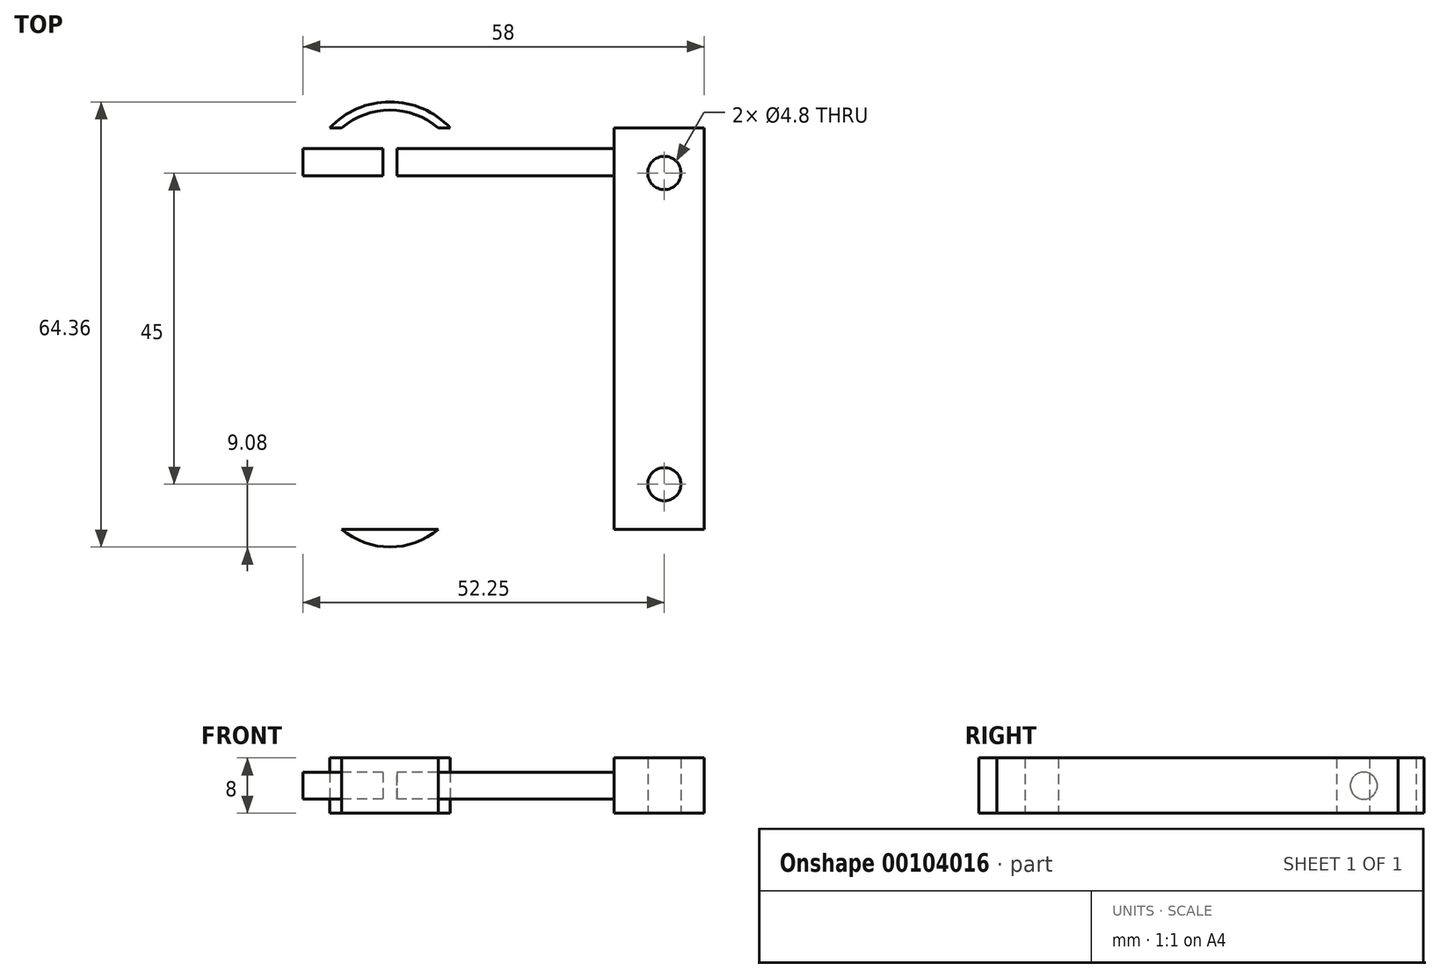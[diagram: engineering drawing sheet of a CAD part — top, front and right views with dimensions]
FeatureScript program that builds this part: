
annotation { "Feature Type Name" : "Feature", "Feature Type Description" : "" }
export const myFeature = defineFeature(function(context is Context, id is Id, definition is map)
    precondition{}
    {
        {
            var Q0;
            Q0=qCreatedBy(makeId("Top.planeOp"),FACE);
            var sketch = newSketch(context, id + "F0", { "sketchPlane" : qUnion([Q0])});
            skLineSegment(sketch, "E0.bottom", {"start": v(29, 29) * mm, "end": v(-29, 29) * mm});
            skLineSegment(sketch, "E0.top", {"start": v(29, -29) * mm, "end": v(-29, -29) * mm});
            skLineSegment(sketch, "E0.left", {"start": v(29, 29) * mm, "end": v(29, -29) * mm});
            skLineSegment(sketch, "E0.right", {"start": v(-29, 29) * mm, "end": v(-29, -29) * mm});
            skPoint(sketch, "E0.middle", {"position": v(0, 0) * mm});
            skCircle(sketch, "E1", {"center": v(-23.25, 0) * mm, "radius": 2.4 * mm});
            skCircle(sketch, "E2", {"center": v(-23.25, 0) * mm, "radius": 11.5 * mm, "construction": true});
            skLineSegment(sketch, "E3", {"start": v(0, 29) * mm, "end": v(0, -29) * mm, "construction": true});
            skCircle(sketch, "E4.MirrorC", {"center": v(23.25, 0) * mm, "radius": 11.5 * mm, "construction": true});
            skCircle(sketch, "E5", {"center": v(23.25, 22.5) * mm, "radius": 2.4 * mm});
            skLineSegment(sketch, "E6", {"start": v(0, 0) * mm, "end": v(29, 0) * mm, "construction": true});
            skCircle(sketch, "E7.MirrorC", {"center": v(23.25, -22.5) * mm, "radius": 2.4 * mm});
            skLineSegment(sketch, "E8", {"start": v(-17.4, 29) * mm, "end": v(-17.4, -29) * mm});
            skLineSegment(sketch, "E9", {"start": v(-15.4, 29) * mm, "end": v(-15.4, -29) * mm});
            skLineSegment(sketch, "E10", {"start": v(-7.76, 17) * mm, "end": v(12.59, 17) * mm});
            skLineSegment(sketch, "E11", {"start": v(12.59, 17) * mm, "end": v(12.59, 14.52) * mm});
            skLineSegment(sketch, "E12", {"start": v(12.59, 14.52) * mm, "end": v(-7.76, 7) * mm});
            skLineSegment(sketch, "E13", {"start": v(-7.76, 7) * mm, "end": v(-7.76, 17) * mm});
            skLineSegment(sketch, "E14.MirrorCS", {"start": v(12.59, -14.52) * mm, "end": v(-7.76, -7) * mm});
            skLineSegment(sketch, "E15.MirrorCS", {"start": v(12.59, -17) * mm, "end": v(12.59, -14.52) * mm});
            skLineSegment(sketch, "E16.MirrorCS", {"start": v(-7.76, -17) * mm, "end": v(12.59, -17) * mm});
            skLineSegment(sketch, "E17.MirrorCS", {"start": v(-7.76, -7) * mm, "end": v(-7.76, -17) * mm});
            skArc(sketch, "E18", {"start": v(-9.41, 29) * mm, "mid": v(-16.4, 31.58) * mm, "end": v(-23.38, 29) * mm});
            skArc(sketch, "E19", {"start": v(-7.68, 29) * mm, "mid": v(-16.4, 32.78) * mm, "end": v(-25.11, 29) * mm});
            skLineSegment(sketch, "E20", {"start": v(-17.4, 20.84) * mm, "end": v(-15.4, 20.84) * mm, "construction": true});
            skArc(sketch, "E21.MirrorCS", {"start": v(-9.41, -29) * mm, "mid": v(-16.4, -31.58) * mm, "end": v(-23.38, -29) * mm});
            skArc(sketch, "E22.MirrorCS", {"start": v(-7.68, -29) * mm, "mid": v(-16.4, -32.78) * mm, "end": v(-25.11, -29) * mm});
            skSolve(sketch);
        }
        {
            var Q0;
            {var subQ0=sQuery(id+"F0.wireOp",EDGE,"E0.right");Q0=makeQuery(id+"F0.imprint","IMPRINT",FACE,{"disambiguationData":[TD([[makeQuery(id+"F0.imprint","IMPRINT",EDGE,{"derivedFrom":subQ0}),1.0]])]});}
            var Q1;
            {var subQ0=sQuery(id+"F0.wireOp",EDGE,"E0.left");Q1=makeQuery(id+"F0.imprint","IMPRINT",FACE,{"disambiguationData":[TD([[makeQuery(id+"F0.imprint","IMPRINT",EDGE,{"derivedFrom":subQ0}),-1.0]])]});}
            var Q2;
            {var subQ0=sQuery(id+"F0.wireOp",EDGE,"E21.MirrorCS");Q2=makeQuery(id+"F0.imprint","IMPRINT",FACE,{"disambiguationData":[TD([[makeQuery(id+"F0.imprint","IMPRINT",EDGE,{"derivedFrom":subQ0}),1.0]])]});}
            var Q3;
            {var subQ0=sQuery(id+"F0.wireOp",EDGE,"E18");Q3=makeQuery(id+"F0.imprint","IMPRINT",FACE,{"disambiguationData":[TD([[makeQuery(id+"F0.imprint","IMPRINT",EDGE,{"derivedFrom":subQ0}),-1.0]])]});}
            extrude(context, id + "F1", {"entities" : qUnion([Q0, Q1, Q2, Q3]), "depth" : 8 * mm});
        }
        {
            var Q0;
            Q0=makeQuery(id+"F1.opExtrude","SWEPT_FACE",FACE,{"disambiguationData":[OSD([sQuery(id+"F0.wireOp",EDGE,"E0.right")])]});
            var sketch = newSketch(context, id + "F2", { "sketchPlane" : qUnion([Q0])});
            skCircle(sketch, "E23", {"center": v(24.05, 4) * mm, "radius": 1.95 * mm});
            skPoint(sketch, "E23.centerSnap0", {"position": v(29, 4) * mm});
            skLineSegment(sketch, "E24", {"start": v(0, 8) * mm, "end": v(0, 0) * mm, "construction": true});
            skCircle(sketch, "E25.MirrorC", {"center": v(-24.05, 4) * mm, "radius": 1.95 * mm});
            skSolve(sketch);
        }
        {
            var Q0;
            Q0=makeQuery(id+"F2.imprint","IMPRINT",FACE,{"disambiguationData":[TD([[makeQuery(id+"F2.imprint","IMPRINT",EDGE,{"derivedFrom":sQuery(id+"F2.wireOp",EDGE,"E23")}),1.0]])]});
            var Q1;
            Q1=makeQuery(id+"F2.imprint","IMPRINT",FACE,{"disambiguationData":[TD([[makeQuery(id+"F2.imprint","IMPRINT",EDGE,{"derivedFrom":sQuery(id+"F2.wireOp",EDGE,"E25.MirrorC")}),-1.0]])]});
            extrude(context, id + "F3", {"entities" : qUnion([Q0, Q1]), "operationType" : NewBodyOperationType.REMOVE, "oppositeDirection" : true, "depth" : 45 * mm});
        }
    });
